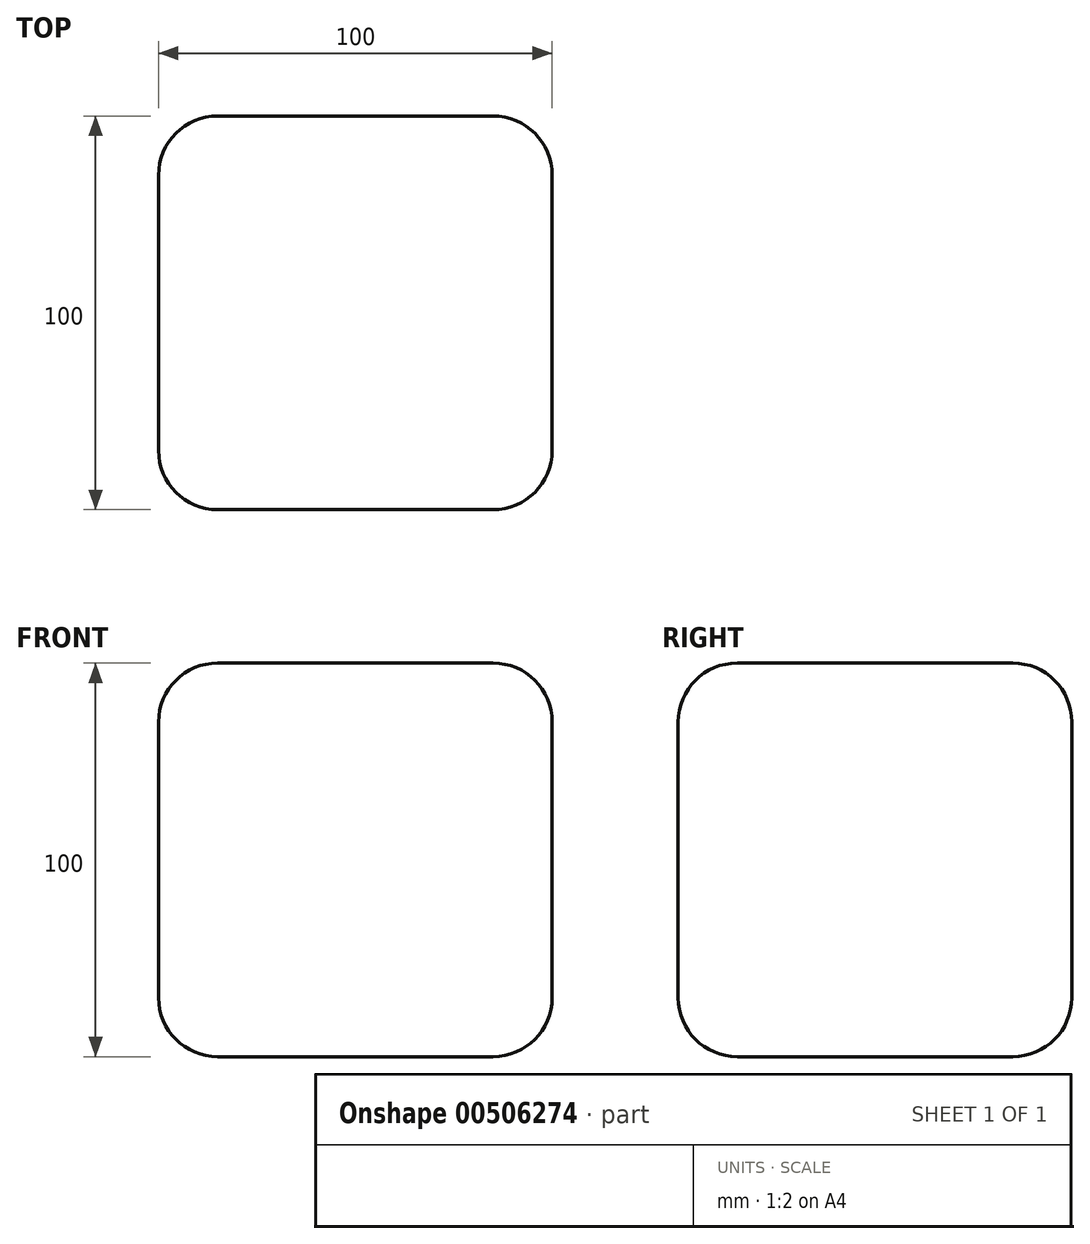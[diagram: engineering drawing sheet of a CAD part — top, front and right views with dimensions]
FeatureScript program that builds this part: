
annotation { "Feature Type Name" : "Feature", "Feature Type Description" : "" }
export const myFeature = defineFeature(function(context is Context, id is Id, definition is map)
    precondition{}
    {
        {
            var Q0;
            Q0=qCreatedBy(makeId("Top.planeOp"),FACE);
            var sketch = newSketch(context, id + "F0", { "sketchPlane" : qUnion([Q0])});
            skLineSegment(sketch, "E0.bottom", {"start": v(-44.85, 60.48) * mm, "end": v(55.15, 60.48) * mm});
            skLineSegment(sketch, "E0.top", {"start": v(-44.85, -39.52) * mm, "end": v(55.15, -39.52) * mm});
            skLineSegment(sketch, "E0.left", {"start": v(-44.85, 60.48) * mm, "end": v(-44.85, -39.52) * mm});
            skLineSegment(sketch, "E0.right", {"start": v(55.15, 60.48) * mm, "end": v(55.15, -39.52) * mm});
            skSolve(sketch);
        }
        {
            var Q0;
            Q0 = qSketchRegion(id + "F0", true);
            extrude(context, id + "F1", {"entities" : qUnion([Q0]), "depth" : 100 * mm});
        }
        {
            var Q0;
            Q0=makeQuery(id+"F1.opExtrude","SWEPT_EDGE",EDGE,{"disambiguationData":[OSD([sQuery(id+"F0.wireOp",EDGE,"E0.bottom"),sQuery(id+"F0.wireOp",EDGE,"E0.left")])]});
            var Q1;
            Q1=makeQuery(id+"F1.opExtrude","CAP_EDGE",EDGE,{"disambiguationData":[OSD([sQuery(id+"F0.wireOp",EDGE,"E0.bottom")])],"isStart":false});
            var Q2;
            Q2=makeQuery(id+"F1.opExtrude","SWEPT_EDGE",EDGE,{"disambiguationData":[OSD([sQuery(id+"F0.wireOp",EDGE,"E0.bottom"),sQuery(id+"F0.wireOp",EDGE,"E0.right")])]});
            var Q3;
            Q3=makeQuery(id+"F1.opExtrude","CAP_EDGE",EDGE,{"disambiguationData":[OSD([sQuery(id+"F0.wireOp",EDGE,"E0.bottom")])],"isStart":true});
            var Q4;
            Q4=makeQuery(id+"F1.opExtrude","CAP_EDGE",EDGE,{"disambiguationData":[OSD([sQuery(id+"F0.wireOp",EDGE,"E0.left")])],"isStart":false});
            var Q5;
            Q5=makeQuery(id+"F1.opExtrude","CAP_EDGE",EDGE,{"disambiguationData":[OSD([sQuery(id+"F0.wireOp",EDGE,"E0.left")])],"isStart":true});
            var Q6;
            Q6=makeQuery(id+"F1.opExtrude","CAP_EDGE",EDGE,{"disambiguationData":[OSD([sQuery(id+"F0.wireOp",EDGE,"E0.right")])],"isStart":false});
            var Q7;
            Q7=makeQuery(id+"F1.opExtrude","CAP_EDGE",EDGE,{"disambiguationData":[OSD([sQuery(id+"F0.wireOp",EDGE,"E0.right")])],"isStart":true});
            var Q8;
            Q8=makeQuery(id+"F1.opExtrude","SWEPT_FACE",FACE,{"disambiguationData":[OSD([sQuery(id+"F0.wireOp",EDGE,"E0.left")])]});
            var Q9;
            Q9=makeQuery(id+"F1.opExtrude","CAP_EDGE",EDGE,{"disambiguationData":[OSD([sQuery(id+"F0.wireOp",EDGE,"E0.top")])],"isStart":true});
            var Q10;
            Q10=makeQuery(id+"F1.opExtrude","SWEPT_EDGE",EDGE,{"disambiguationData":[OSD([sQuery(id+"F0.wireOp",EDGE,"E0.top"),sQuery(id+"F0.wireOp",EDGE,"E0.right")])]});
            var Q11;
            Q11=makeQuery(id+"F1.opExtrude","SWEPT_FACE",FACE,{"disambiguationData":[OSD([sQuery(id+"F0.wireOp",EDGE,"E0.top")])]});
            fillet(context, id + "F2", {"entities" : qUnion([Q0, Q1, Q2, Q3, Q4, Q5, Q6, Q7, Q8, Q9, Q10, Q11]), "radius" : 15 * mm, "tangentPropagation" : true, "allowEdgeOverflow" : false});
        }
    });
